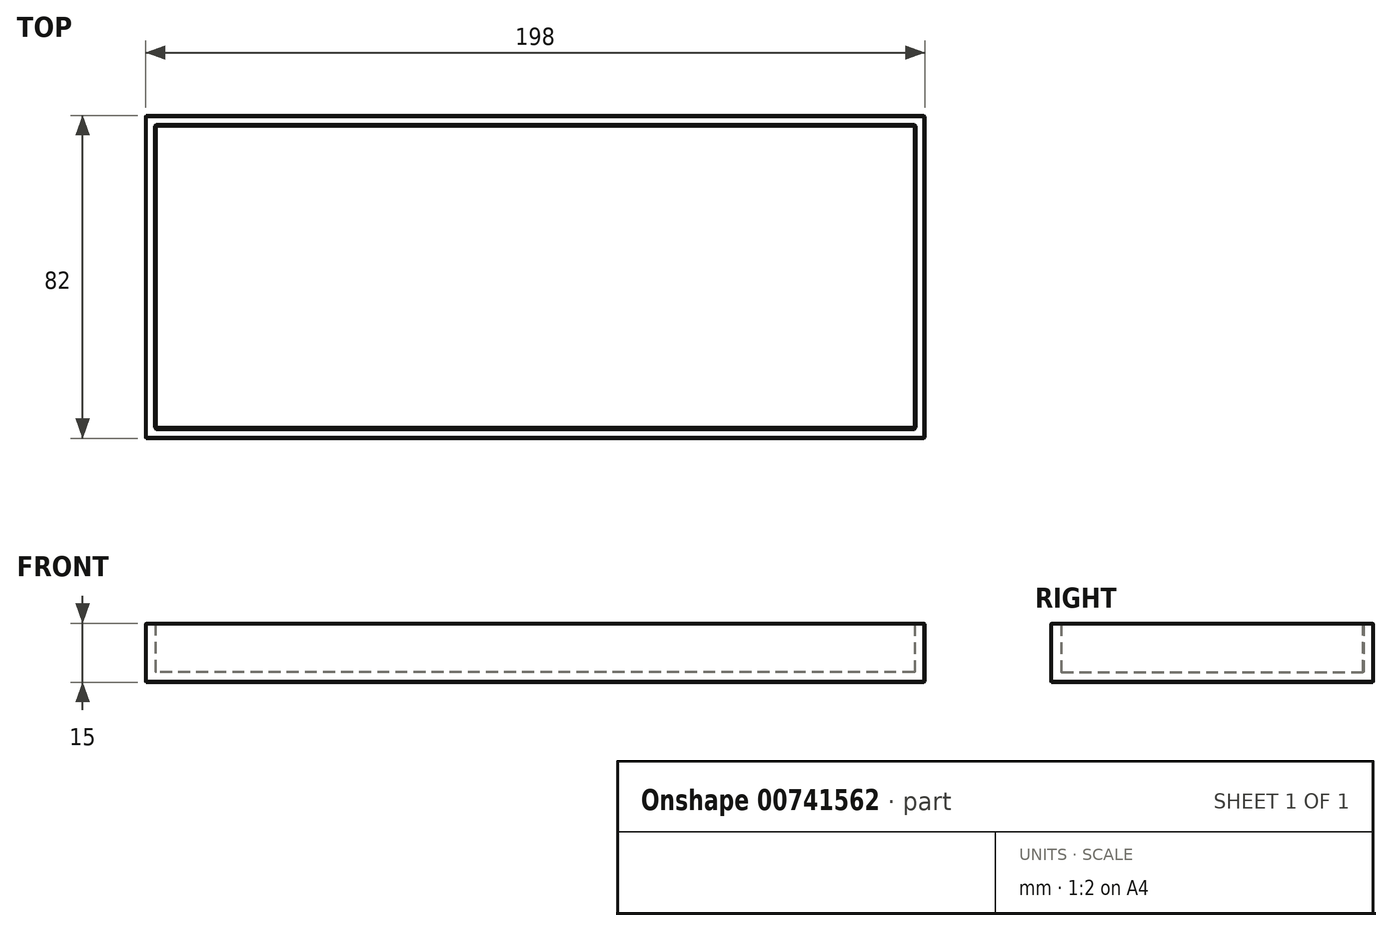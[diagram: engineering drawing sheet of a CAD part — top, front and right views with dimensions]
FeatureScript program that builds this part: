
annotation { "Feature Type Name" : "Feature", "Feature Type Description" : "" }
export const myFeature = defineFeature(function(context is Context, id is Id, definition is map)
    precondition{}
    {
        {
            var Q0;
            Q0=qCreatedBy(makeId("Top.planeOp"),FACE);
            var sketch = newSketch(context, id + "F0", { "sketchPlane" : qUnion([Q0])});
            skLineSegment(sketch, "E0.bottom", {"start": v(-99, -41) * mm, "end": v(99, -41) * mm});
            skLineSegment(sketch, "E0.top", {"start": v(-99, 41) * mm, "end": v(99, 41) * mm});
            skLineSegment(sketch, "E0.left", {"start": v(-99, -41) * mm, "end": v(-99, 41) * mm});
            skLineSegment(sketch, "E0.right", {"start": v(99, -41) * mm, "end": v(99, 41) * mm});
            skPoint(sketch, "E0.middle", {"position": v(0, 0) * mm});
            skSolve(sketch);
        }
        {
            var Q0;
            Q0=makeQuery(id+"F0.imprint","IMPRINT",FACE,{"disambiguationData":[TD([[makeQuery(id+"F0.imprint","IMPRINT",EDGE,{"derivedFrom":sQuery(id+"F0.wireOp",EDGE,"E0.bottom")}),1.0]])]});
            extrude(context, id + "F1", {"entities" : qUnion([Q0]), "depth" : 15 * mm, "offsetDistance" : 25 * mm});
        }
        {
            var Q0;
            Q0=makeQuery(id+"F1.opExtrude","CAP_FACE",FACE,{"disambiguationData":[OSD([sQuery(id+"F0.wireOp",EDGE,"E0.bottom"),sQuery(id+"F0.wireOp",EDGE,"E0.top"),sQuery(id+"F0.wireOp",EDGE,"E0.left"),sQuery(id+"F0.wireOp",EDGE,"E0.right")])],"isStart":false});
            shell(context, id + "F2", {"entities" : qUnion([Q0]), "thickness" : 2.5 * mm});
        }
        {
            var Q0;
            Q0=makeQuery(id+"F1.opExtrude","SWEPT_EDGE",EDGE,{"disambiguationData":[OSD([sQuery(id+"F0.wireOp",EDGE,"E0.top"),sQuery(id+"F0.wireOp",EDGE,"E0.right")])]});
            var Q1;
            Q1=makeQuery(id+"F1.opExtrude","SWEPT_EDGE",EDGE,{"disambiguationData":[OSD([sQuery(id+"F0.wireOp",EDGE,"E0.bottom"),sQuery(id+"F0.wireOp",EDGE,"E0.right")])]});
            var Q2;
            Q2=makeQuery(id+"F1.opExtrude","SWEPT_EDGE",EDGE,{"disambiguationData":[OSD([sQuery(id+"F0.wireOp",EDGE,"E0.bottom"),sQuery(id+"F0.wireOp",EDGE,"E0.left")])]});
            var Q3;
            Q3=makeQuery(id+"F1.opExtrude","CAP_EDGE",EDGE,{"disambiguationData":[OSD([sQuery(id+"F0.wireOp",EDGE,"E0.bottom")])],"isStart":true});
            var Q4;
            Q4=makeQuery(id+"F1.opExtrude","CAP_EDGE",EDGE,{"disambiguationData":[OSD([sQuery(id+"F0.wireOp",EDGE,"E0.bottom")])],"isStart":false});
            var Q5;
            Q5=makeQuery(id+"F1.opExtrude","CAP_EDGE",EDGE,{"disambiguationData":[OSD([sQuery(id+"F0.wireOp",EDGE,"E0.top")])],"isStart":false});
            var Q6;
            Q6=makeQuery(id+"F1.opExtrude","CAP_EDGE",EDGE,{"disambiguationData":[OSD([sQuery(id+"F0.wireOp",EDGE,"E0.left")])],"isStart":false});
            var Q7;
            Q7=makeQuery(id+"F1.opExtrude","CAP_EDGE",EDGE,{"disambiguationData":[OSD([sQuery(id+"F0.wireOp",EDGE,"E0.right")])],"isStart":true});
            var Q8;
            Q8=makeQuery(id+"F1.opExtrude","CAP_EDGE",EDGE,{"disambiguationData":[OSD([sQuery(id+"F0.wireOp",EDGE,"E0.right")])],"isStart":false});
            var Q9;
            Q9=makeQuery(id+"F2.opShell","OFFSET_EDGE",EDGE,{"disambiguationData":[OSD([sQuery(id+"F0.wireOp",EDGE,"E0.top"),sQuery(id+"F0.wireOp",EDGE,"E0.left")])]});
            var Q10;
            {var subQ0=sQuery(id+"F0.wireOp",EDGE,"E0.bottom");Q10=makeQuery(id+"F2.opShell","OFFSET_EDGE",EDGE,{"disambiguationData":[OSD([subQ0]),TDD([makeQuery(id+"F1.opExtrude","CAP_EDGE",EDGE,{"disambiguationData":[OSD([subQ0])],"isStart":false})])]});}
            var Q11;
            {var subQ0=sQuery(id+"F0.wireOp",EDGE,"E0.top");Q11=makeQuery(id+"F2.opShell","OFFSET_EDGE",EDGE,{"disambiguationData":[OSD([subQ0]),TDD([makeQuery(id+"F1.opExtrude","CAP_EDGE",EDGE,{"disambiguationData":[OSD([subQ0])],"isStart":true})])]});}
            var Q12;
            {var subQ0=sQuery(id+"F0.wireOp",EDGE,"E0.top");Q12=makeQuery(id+"F2.opShell","OFFSET_EDGE",EDGE,{"disambiguationData":[OSD([subQ0]),TDD([makeQuery(id+"F1.opExtrude","CAP_EDGE",EDGE,{"disambiguationData":[OSD([subQ0])],"isStart":false})])]});}
            var Q13;
            {var subQ0=sQuery(id+"F0.wireOp",EDGE,"E0.left");Q13=makeQuery(id+"F2.opShell","OFFSET_EDGE",EDGE,{"disambiguationData":[OSD([subQ0]),TDD([makeQuery(id+"F1.opExtrude","CAP_EDGE",EDGE,{"disambiguationData":[OSD([subQ0])],"isStart":true})])]});}
            var Q14;
            {var subQ0=sQuery(id+"F0.wireOp",EDGE,"E0.left");Q14=makeQuery(id+"F2.opShell","OFFSET_EDGE",EDGE,{"disambiguationData":[OSD([subQ0]),TDD([makeQuery(id+"F1.opExtrude","CAP_EDGE",EDGE,{"disambiguationData":[OSD([subQ0])],"isStart":false})])]});}
            var Q15;
            {var subQ0=sQuery(id+"F0.wireOp",EDGE,"E0.right");Q15=makeQuery(id+"F2.opShell","OFFSET_EDGE",EDGE,{"disambiguationData":[OSD([subQ0]),TDD([makeQuery(id+"F1.opExtrude","CAP_EDGE",EDGE,{"disambiguationData":[OSD([subQ0])],"isStart":false})])]});}
            var Q16;
            Q16=makeQuery(id+"F1.opExtrude","SWEPT_EDGE",EDGE,{"disambiguationData":[OSD([sQuery(id+"F0.wireOp",EDGE,"E0.top"),sQuery(id+"F0.wireOp",EDGE,"E0.left")])]});
            var Q17;
            Q17=makeQuery(id+"F1.opExtrude","CAP_EDGE",EDGE,{"disambiguationData":[OSD([sQuery(id+"F0.wireOp",EDGE,"E0.top")])],"isStart":true});
            var Q18;
            Q18=makeQuery(id+"F1.opExtrude","CAP_EDGE",EDGE,{"disambiguationData":[OSD([sQuery(id+"F0.wireOp",EDGE,"E0.left")])],"isStart":true});
            var Q19;
            Q19=makeQuery(id+"F2.opShell","OFFSET_EDGE",EDGE,{"disambiguationData":[OSD([sQuery(id+"F0.wireOp",EDGE,"E0.bottom"),sQuery(id+"F0.wireOp",EDGE,"E0.left")])]});
            var Q20;
            Q20=makeQuery(id+"F2.opShell","OFFSET_EDGE",EDGE,{"disambiguationData":[OSD([sQuery(id+"F0.wireOp",EDGE,"E0.bottom"),sQuery(id+"F0.wireOp",EDGE,"E0.right")])]});
            var Q21;
            Q21=makeQuery(id+"F2.opShell","OFFSET_EDGE",EDGE,{"disambiguationData":[OSD([sQuery(id+"F0.wireOp",EDGE,"E0.top"),sQuery(id+"F0.wireOp",EDGE,"E0.right")])]});
            var Q22;
            {var subQ0=sQuery(id+"F0.wireOp",EDGE,"E0.bottom");Q22=makeQuery(id+"F2.opShell","OFFSET_EDGE",EDGE,{"disambiguationData":[OSD([subQ0]),TDD([makeQuery(id+"F1.opExtrude","CAP_EDGE",EDGE,{"disambiguationData":[OSD([subQ0])],"isStart":true})])]});}
            var Q23;
            {var subQ0=sQuery(id+"F0.wireOp",EDGE,"E0.right");Q23=makeQuery(id+"F2.opShell","OFFSET_EDGE",EDGE,{"disambiguationData":[OSD([subQ0]),TDD([makeQuery(id+"F1.opExtrude","CAP_EDGE",EDGE,{"disambiguationData":[OSD([subQ0])],"isStart":true})])]});}
            chamfer(context, id + "F3", {"entities" : qUnion([Q0, Q1, Q2, Q3, Q4, Q5, Q6, Q7, Q8, Q9, Q10, Q11, Q12, Q13, Q14, Q15, Q16, Q17, Q18, Q19, Q20, Q21, Q22, Q23]), "width" : 0.2 * mm, "tangentPropagation" : true});
        }
    });
